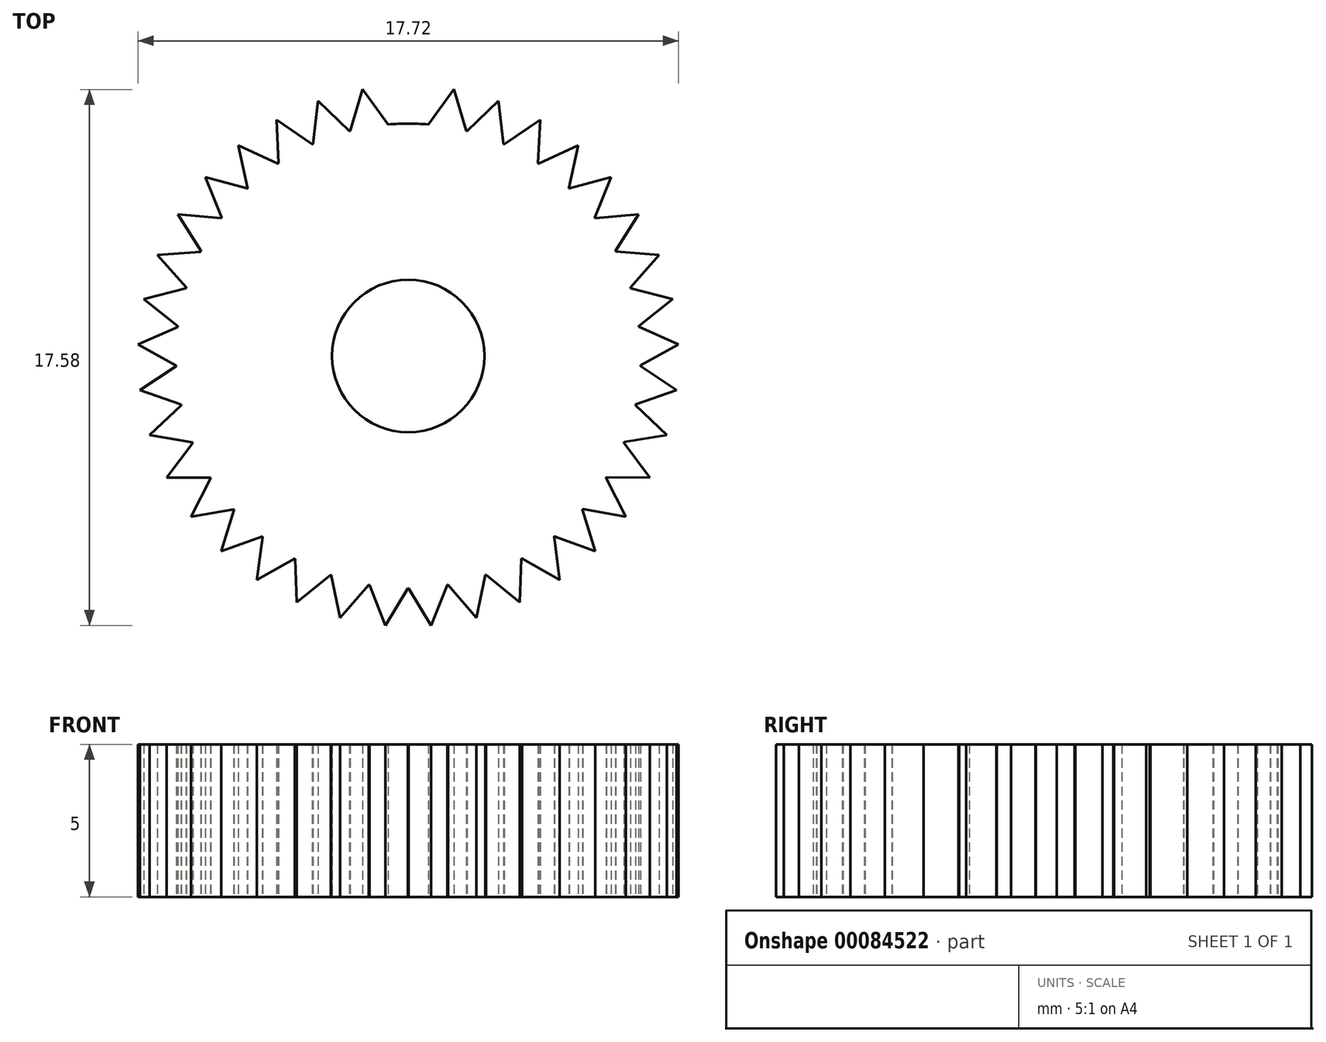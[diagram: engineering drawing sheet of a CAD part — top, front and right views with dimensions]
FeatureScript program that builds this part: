
annotation { "Feature Type Name" : "Feature", "Feature Type Description" : "" }
export const myFeature = defineFeature(function(context is Context, id is Id, definition is map)
    precondition{}
    {
        {
            var Q0;
            Q0=qCreatedBy(makeId("Top.planeOp"),FACE);
            var sketch = newSketch(context, id + "F0", { "sketchPlane" : qUnion([Q0])});
            skCircle(sketch, "E0", {"center": v(0, 0) * mm, "radius": 2.5 * mm});
            skPoint(sketch, "E1", {"position": v(0, 7.62) * mm});
            skLineSegment(sketch, "E2", {"start": v(0, 8.87) * mm, "end": v(-0.64, 7.6) * mm});
            skLineSegment(sketch, "E3", {"start": v(0, 8.87) * mm, "end": v(0.63, 7.6) * mm});
            skLineSegment(sketch, "E4.1.0", {"start": v(1.5, 8.74) * mm, "end": v(1.9, 7.38) * mm});
            skLineSegment(sketch, "E4.1.1", {"start": v(1.5, 8.74) * mm, "end": v(0.66, 7.6) * mm});
            skLineSegment(sketch, "E4.2.0", {"start": v(2.95, 8.36) * mm, "end": v(3.13, 6.95) * mm});
            skLineSegment(sketch, "E4.2.1", {"start": v(2.95, 8.36) * mm, "end": v(1.93, 7.37) * mm});
            skLineSegment(sketch, "E4.3.0", {"start": v(4.33, 7.74) * mm, "end": v(4.26, 6.32) * mm});
            skLineSegment(sketch, "E4.3.1", {"start": v(4.33, 7.74) * mm, "end": v(3.15, 6.94) * mm});
            skLineSegment(sketch, "E4.4.0", {"start": v(5.57, 6.9) * mm, "end": v(5.26, 5.51) * mm});
            skLineSegment(sketch, "E4.4.1", {"start": v(5.57, 6.9) * mm, "end": v(4.27, 6.3) * mm});
            skLineSegment(sketch, "E4.5.0", {"start": v(6.66, 5.86) * mm, "end": v(6.12, 4.54) * mm});
            skLineSegment(sketch, "E4.5.1", {"start": v(6.66, 5.86) * mm, "end": v(5.28, 5.5) * mm});
            skLineSegment(sketch, "E4.6.0", {"start": v(7.55, 4.65) * mm, "end": v(6.8, 3.44) * mm});
            skLineSegment(sketch, "E4.6.1", {"start": v(7.55, 4.65) * mm, "end": v(6.13, 4.52) * mm});
            skLineSegment(sketch, "E4.7.0", {"start": v(8.23, 3.3) * mm, "end": v(7.28, 2.24) * mm});
            skLineSegment(sketch, "E4.7.1", {"start": v(8.23, 3.3) * mm, "end": v(6.8, 3.42) * mm});
            skLineSegment(sketch, "E4.8.0", {"start": v(8.67, 1.87) * mm, "end": v(7.56, 0.98) * mm});
            skLineSegment(sketch, "E4.8.1", {"start": v(8.67, 1.87) * mm, "end": v(7.29, 2.22) * mm});
            skLineSegment(sketch, "E4.9.0", {"start": v(8.86, 0.38) * mm, "end": v(7.61, -0.3) * mm});
            skLineSegment(sketch, "E4.9.1", {"start": v(8.86, 0.38) * mm, "end": v(7.56, 0.96) * mm});
            skLineSegment(sketch, "E4.10.0", {"start": v(8.8, -1.13) * mm, "end": v(7.45, -1.6) * mm});
            skLineSegment(sketch, "E4.10.1", {"start": v(8.8, -1.13) * mm, "end": v(7.61, -0.33) * mm});
            skLineSegment(sketch, "E4.11.0", {"start": v(8.48, -2.6) * mm, "end": v(7.08, -2.83) * mm});
            skLineSegment(sketch, "E4.11.1", {"start": v(8.48, -2.6) * mm, "end": v(7.45, -1.61) * mm});
            skLineSegment(sketch, "E4.12.0", {"start": v(7.92, -4) * mm, "end": v(6.5, -3.98) * mm});
            skLineSegment(sketch, "E4.12.1", {"start": v(7.92, -4) * mm, "end": v(7.07, -2.85) * mm});
            skLineSegment(sketch, "E4.13.0", {"start": v(7.13, -5.27) * mm, "end": v(5.73, -5.02) * mm});
            skLineSegment(sketch, "E4.13.1", {"start": v(7.13, -5.27) * mm, "end": v(6.48, -4) * mm});
            skLineSegment(sketch, "E4.14.0", {"start": v(6.14, -6.4) * mm, "end": v(4.8, -5.92) * mm});
            skLineSegment(sketch, "E4.14.1", {"start": v(6.14, -6.4) * mm, "end": v(5.71, -5.04) * mm});
            skLineSegment(sketch, "E4.15.0", {"start": v(4.97, -7.35) * mm, "end": v(3.73, -6.65) * mm});
            skLineSegment(sketch, "E4.15.1", {"start": v(4.97, -7.35) * mm, "end": v(4.78, -5.93) * mm});
            skLineSegment(sketch, "E4.16.0", {"start": v(3.65, -8.08) * mm, "end": v(2.55, -7.18) * mm});
            skLineSegment(sketch, "E4.16.1", {"start": v(3.65, -8.08) * mm, "end": v(3.7, -6.66) * mm});
            skLineSegment(sketch, "E4.17.0", {"start": v(2.24, -8.58) * mm, "end": v(1.3, -7.5) * mm});
            skLineSegment(sketch, "E4.17.1", {"start": v(2.24, -8.58) * mm, "end": v(2.53, -7.19) * mm});
            skLineSegment(sketch, "E4.18.0", {"start": v(0.75, -8.84) * mm, "end": v(0.01, -7.62) * mm});
            skLineSegment(sketch, "E4.18.1", {"start": v(0.75, -8.84) * mm, "end": v(1.28, -7.51) * mm});
            skLineSegment(sketch, "E4.19.0", {"start": v(-0.75, -8.84) * mm, "end": v(-1.27, -7.51) * mm});
            skLineSegment(sketch, "E4.19.1", {"start": v(-0.75, -8.84) * mm, "end": v(0, -7.62) * mm});
            skLineSegment(sketch, "E4.20.0", {"start": v(-2.24, -8.58) * mm, "end": v(-2.53, -7.19) * mm});
            skLineSegment(sketch, "E4.20.1", {"start": v(-2.24, -8.58) * mm, "end": v(-1.3, -7.5) * mm});
            skLineSegment(sketch, "E4.21.0", {"start": v(-3.65, -8.08) * mm, "end": v(-3.7, -6.66) * mm});
            skLineSegment(sketch, "E4.21.1", {"start": v(-3.65, -8.08) * mm, "end": v(-2.55, -7.18) * mm});
            skLineSegment(sketch, "E4.22.0", {"start": v(-4.97, -7.35) * mm, "end": v(-4.78, -5.94) * mm});
            skLineSegment(sketch, "E4.22.1", {"start": v(-4.97, -7.35) * mm, "end": v(-3.72, -6.65) * mm});
            skLineSegment(sketch, "E4.23.0", {"start": v(-6.14, -6.4) * mm, "end": v(-5.71, -5.04) * mm});
            skLineSegment(sketch, "E4.23.1", {"start": v(-6.14, -6.4) * mm, "end": v(-4.8, -5.92) * mm});
            skLineSegment(sketch, "E4.24.0", {"start": v(-7.13, -5.27) * mm, "end": v(-6.48, -4) * mm});
            skLineSegment(sketch, "E4.24.1", {"start": v(-7.13, -5.27) * mm, "end": v(-5.73, -5.03) * mm});
            skLineSegment(sketch, "E4.25.0", {"start": v(-7.92, -4) * mm, "end": v(-7.07, -2.85) * mm});
            skLineSegment(sketch, "E4.25.1", {"start": v(-7.92, -4) * mm, "end": v(-6.5, -3.99) * mm});
            skLineSegment(sketch, "E4.26.0", {"start": v(-8.48, -2.6) * mm, "end": v(-7.45, -1.62) * mm});
            skLineSegment(sketch, "E4.26.1", {"start": v(-8.48, -2.6) * mm, "end": v(-7.07, -2.83) * mm});
            skLineSegment(sketch, "E4.27.0", {"start": v(-8.8, -1.13) * mm, "end": v(-7.61, -0.34) * mm});
            skLineSegment(sketch, "E4.27.1", {"start": v(-8.8, -1.13) * mm, "end": v(-7.45, -1.6) * mm});
            skLineSegment(sketch, "E4.28.0", {"start": v(-8.86, 0.38) * mm, "end": v(-7.56, 0.95) * mm});
            skLineSegment(sketch, "E4.28.1", {"start": v(-8.86, 0.38) * mm, "end": v(-7.61, -0.31) * mm});
            skLineSegment(sketch, "E4.29.0", {"start": v(-8.67, 1.87) * mm, "end": v(-7.29, 2.22) * mm});
            skLineSegment(sketch, "E4.29.1", {"start": v(-8.67, 1.87) * mm, "end": v(-7.56, 0.98) * mm});
            skLineSegment(sketch, "E4.30.0", {"start": v(-8.23, 3.3) * mm, "end": v(-6.81, 3.42) * mm});
            skLineSegment(sketch, "E4.30.1", {"start": v(-8.23, 3.3) * mm, "end": v(-7.28, 2.24) * mm});
            skLineSegment(sketch, "E4.31.0", {"start": v(-7.55, 4.65) * mm, "end": v(-6.13, 4.52) * mm});
            skLineSegment(sketch, "E4.31.1", {"start": v(-7.55, 4.65) * mm, "end": v(-6.8, 3.44) * mm});
            skLineSegment(sketch, "E4.32.0", {"start": v(-6.66, 5.86) * mm, "end": v(-5.28, 5.5) * mm});
            skLineSegment(sketch, "E4.32.1", {"start": v(-6.66, 5.86) * mm, "end": v(-6.12, 4.54) * mm});
            skLineSegment(sketch, "E4.33.0", {"start": v(-5.57, 6.9) * mm, "end": v(-4.28, 6.3) * mm});
            skLineSegment(sketch, "E4.33.1", {"start": v(-5.57, 6.9) * mm, "end": v(-5.27, 5.5) * mm});
            skLineSegment(sketch, "E4.34.0", {"start": v(-4.33, 7.74) * mm, "end": v(-3.15, 6.94) * mm});
            skLineSegment(sketch, "E4.34.1", {"start": v(-4.33, 7.74) * mm, "end": v(-4.26, 6.32) * mm});
            skLineSegment(sketch, "E4.35.0", {"start": v(-2.95, 8.36) * mm, "end": v(-1.93, 7.37) * mm});
            skLineSegment(sketch, "E4.35.1", {"start": v(-2.95, 8.36) * mm, "end": v(-3.13, 6.95) * mm});
            skLineSegment(sketch, "E4.36.0", {"start": v(-1.5, 8.74) * mm, "end": v(-0.66, 7.6) * mm});
            skLineSegment(sketch, "E4.36.1", {"start": v(-1.5, 8.74) * mm, "end": v(-1.91, 7.38) * mm});
            skCircle(sketch, "E5", {"center": v(0, 0) * mm, "radius": 7.62 * mm});
            skLineSegment(sketch, "E6", {"start": v(-0.64, 7.6) * mm, "end": v(0, 8.87) * mm});
            skSolve(sketch);
        }
        {
            var Q0;
            Q0=makeQuery(id+"F0.imprint","IMPRINT",FACE,{"disambiguationData":[TD([[makeQuery(id+"F0.imprint","IMPRINT",EDGE,{"derivedFrom":sQuery(id+"F0.wireOp",EDGE,"E0")}),-1.0]])]});
            var Q1;
            {var subQ0=sQuery(id+"F0.wireOp",EDGE,"E4.32.0");Q1=makeQuery(id+"F0.imprint","IMPRINT",FACE,{"disambiguationData":[TD([[makeQuery(id+"F0.imprint","IMPRINT",EDGE,{"derivedFrom":subQ0}),-1.0]])]});}
            var Q2;
            {var subQ0=sQuery(id+"F0.wireOp",EDGE,"E4.33.0");Q2=makeQuery(id+"F0.imprint","IMPRINT",FACE,{"disambiguationData":[TD([[makeQuery(id+"F0.imprint","IMPRINT",EDGE,{"derivedFrom":subQ0}),-1.0]])]});}
            var Q3;
            {var subQ0=sQuery(id+"F0.wireOp",EDGE,"E4.34.0");Q3=makeQuery(id+"F0.imprint","IMPRINT",FACE,{"disambiguationData":[TD([[makeQuery(id+"F0.imprint","IMPRINT",EDGE,{"derivedFrom":subQ0}),-1.0]])]});}
            var Q4;
            {var subQ0=sQuery(id+"F0.wireOp",EDGE,"E4.35.0");Q4=makeQuery(id+"F0.imprint","IMPRINT",FACE,{"disambiguationData":[TD([[makeQuery(id+"F0.imprint","IMPRINT",EDGE,{"derivedFrom":subQ0}),-1.0]])]});}
            var Q5;
            {var subQ0=sQuery(id+"F0.wireOp",EDGE,"E4.36.0");Q5=makeQuery(id+"F0.imprint","IMPRINT",FACE,{"disambiguationData":[TD([[makeQuery(id+"F0.imprint","IMPRINT",EDGE,{"derivedFrom":subQ0}),-1.0]])]});}
            var Q6;
            {var subQ0=sQuery(id+"F0.wireOp",EDGE,"E4.1.0");Q6=makeQuery(id+"F0.imprint","IMPRINT",FACE,{"disambiguationData":[TD([[makeQuery(id+"F0.imprint","IMPRINT",EDGE,{"derivedFrom":subQ0}),-1.0]])]});}
            var Q7;
            {var subQ0=sQuery(id+"F0.wireOp",EDGE,"E4.2.0");Q7=makeQuery(id+"F0.imprint","IMPRINT",FACE,{"disambiguationData":[TD([[makeQuery(id+"F0.imprint","IMPRINT",EDGE,{"derivedFrom":subQ0}),-1.0]])]});}
            var Q8;
            {var subQ0=sQuery(id+"F0.wireOp",EDGE,"pScTJWKr-x1fD-1paM-wDNM-PNdl5gfp4UO0");Q8=makeQuery(id+"F0.imprint","IMPRINT",FACE,{"disambiguationData":[TD([[makeQuery(id+"F0.imprint","IMPRINT",EDGE,{"derivedFrom":subQ0}),-1.0]])]});}
            var Q9;
            {var subQ0=sQuery(id+"F0.wireOp",EDGE,"pScTJWKr-x1fD-1paM-wDNM-PNdl5gfp4UO0");Q9=makeQuery(id+"F0.imprint","IMPRINT",FACE,{"disambiguationData":[TD([[makeQuery(id+"F0.imprint","IMPRINT",EDGE,{"derivedFrom":subQ0}),1.0]])]});}
            var Q10;
            {var subQ0=sQuery(id+"F0.wireOp",EDGE,"E4.3.0");Q10=makeQuery(id+"F0.imprint","IMPRINT",FACE,{"disambiguationData":[TD([[makeQuery(id+"F0.imprint","IMPRINT",EDGE,{"derivedFrom":subQ0}),-1.0]])]});}
            var Q11;
            {var subQ0=sQuery(id+"F0.wireOp",EDGE,"E4.4.0");Q11=makeQuery(id+"F0.imprint","IMPRINT",FACE,{"disambiguationData":[TD([[makeQuery(id+"F0.imprint","IMPRINT",EDGE,{"derivedFrom":subQ0}),-1.0]])]});}
            var Q12;
            {var subQ0=sQuery(id+"F0.wireOp",EDGE,"E4.5.0");Q12=makeQuery(id+"F0.imprint","IMPRINT",FACE,{"disambiguationData":[TD([[makeQuery(id+"F0.imprint","IMPRINT",EDGE,{"derivedFrom":subQ0}),-1.0]])]});}
            var Q13;
            {var subQ0=sQuery(id+"F0.wireOp",EDGE,"E4.6.0");Q13=makeQuery(id+"F0.imprint","IMPRINT",FACE,{"disambiguationData":[TD([[makeQuery(id+"F0.imprint","IMPRINT",EDGE,{"derivedFrom":subQ0}),-1.0]])]});}
            var Q14;
            {var subQ1=sQuery(id+"F0.wireOp",EDGE,"E4.7.0");Q14=makeQuery(id+"F0.imprint","IMPRINT",FACE,{"disambiguationData":[TD([[makeQuery(id+"F0.imprint","IMPRINT",EDGE,{"derivedFrom":subQ1}),-1.0]])]});}
            var Q15;
            {var subQ0=sQuery(id+"F0.wireOp",EDGE,"E4.8.0");Q15=makeQuery(id+"F0.imprint","IMPRINT",FACE,{"disambiguationData":[TD([[makeQuery(id+"F0.imprint","IMPRINT",EDGE,{"derivedFrom":subQ0}),-1.0]])]});}
            var Q16;
            {var subQ1=sQuery(id+"F0.wireOp",EDGE,"E4.9.0");Q16=makeQuery(id+"F0.imprint","IMPRINT",FACE,{"disambiguationData":[TD([[makeQuery(id+"F0.imprint","IMPRINT",EDGE,{"derivedFrom":subQ1}),-1.0]])]});}
            var Q17;
            {var subQ1=sQuery(id+"F0.wireOp",EDGE,"E4.10.0");Q17=makeQuery(id+"F0.imprint","IMPRINT",FACE,{"disambiguationData":[TD([[makeQuery(id+"F0.imprint","IMPRINT",EDGE,{"derivedFrom":subQ1}),-1.0]])]});}
            var Q18;
            {var subQ0=sQuery(id+"F0.wireOp",EDGE,"E4.11.0");Q18=makeQuery(id+"F0.imprint","IMPRINT",FACE,{"disambiguationData":[TD([[makeQuery(id+"F0.imprint","IMPRINT",EDGE,{"derivedFrom":subQ0}),-1.0]])]});}
            var Q19;
            {var subQ1=sQuery(id+"F0.wireOp",EDGE,"E4.12.0");Q19=makeQuery(id+"F0.imprint","IMPRINT",FACE,{"disambiguationData":[TD([[makeQuery(id+"F0.imprint","IMPRINT",EDGE,{"derivedFrom":subQ1}),-1.0]])]});}
            var Q20;
            {var subQ0=sQuery(id+"F0.wireOp",EDGE,"E4.13.0");Q20=makeQuery(id+"F0.imprint","IMPRINT",FACE,{"disambiguationData":[TD([[makeQuery(id+"F0.imprint","IMPRINT",EDGE,{"derivedFrom":subQ0}),-1.0]])]});}
            var Q21;
            {var subQ0=sQuery(id+"F0.wireOp",EDGE,"E4.14.0");Q21=makeQuery(id+"F0.imprint","IMPRINT",FACE,{"disambiguationData":[TD([[makeQuery(id+"F0.imprint","IMPRINT",EDGE,{"derivedFrom":subQ0}),-1.0]])]});}
            var Q22;
            {var subQ0=sQuery(id+"F0.wireOp",EDGE,"E4.15.0");Q22=makeQuery(id+"F0.imprint","IMPRINT",FACE,{"disambiguationData":[TD([[makeQuery(id+"F0.imprint","IMPRINT",EDGE,{"derivedFrom":subQ0}),-1.0]])]});}
            var Q23;
            {var subQ0=sQuery(id+"F0.wireOp",EDGE,"E4.16.0");Q23=makeQuery(id+"F0.imprint","IMPRINT",FACE,{"disambiguationData":[TD([[makeQuery(id+"F0.imprint","IMPRINT",EDGE,{"derivedFrom":subQ0}),-1.0]])]});}
            var Q24;
            {var subQ0=sQuery(id+"F0.wireOp",EDGE,"E4.17.0");Q24=makeQuery(id+"F0.imprint","IMPRINT",FACE,{"disambiguationData":[TD([[makeQuery(id+"F0.imprint","IMPRINT",EDGE,{"derivedFrom":subQ0}),-1.0]])]});}
            var Q25;
            {var subQ0=sQuery(id+"F0.wireOp",EDGE,"E4.18.0");Q25=makeQuery(id+"F0.imprint","IMPRINT",FACE,{"disambiguationData":[TD([[makeQuery(id+"F0.imprint","IMPRINT",EDGE,{"derivedFrom":subQ0}),-1.0]])]});}
            var Q26;
            {var subQ0=sQuery(id+"F0.wireOp",EDGE,"E4.19.0");Q26=makeQuery(id+"F0.imprint","IMPRINT",FACE,{"disambiguationData":[TD([[makeQuery(id+"F0.imprint","IMPRINT",EDGE,{"derivedFrom":subQ0}),-1.0]])]});}
            var Q27;
            {var subQ1=sQuery(id+"F0.wireOp",EDGE,"E4.20.0");Q27=makeQuery(id+"F0.imprint","IMPRINT",FACE,{"disambiguationData":[TD([[makeQuery(id+"F0.imprint","IMPRINT",EDGE,{"derivedFrom":subQ1}),-1.0]])]});}
            var Q28;
            {var subQ0=sQuery(id+"F0.wireOp",EDGE,"E4.21.0");Q28=makeQuery(id+"F0.imprint","IMPRINT",FACE,{"disambiguationData":[TD([[makeQuery(id+"F0.imprint","IMPRINT",EDGE,{"derivedFrom":subQ0}),-1.0]])]});}
            var Q29;
            {var subQ0=sQuery(id+"F0.wireOp",EDGE,"E4.22.0");Q29=makeQuery(id+"F0.imprint","IMPRINT",FACE,{"disambiguationData":[TD([[makeQuery(id+"F0.imprint","IMPRINT",EDGE,{"derivedFrom":subQ0}),-1.0]])]});}
            var Q30;
            {var subQ0=sQuery(id+"F0.wireOp",EDGE,"E4.23.0");Q30=makeQuery(id+"F0.imprint","IMPRINT",FACE,{"disambiguationData":[TD([[makeQuery(id+"F0.imprint","IMPRINT",EDGE,{"derivedFrom":subQ0}),-1.0]])]});}
            var Q31;
            {var subQ0=sQuery(id+"F0.wireOp",EDGE,"E4.24.0");Q31=makeQuery(id+"F0.imprint","IMPRINT",FACE,{"disambiguationData":[TD([[makeQuery(id+"F0.imprint","IMPRINT",EDGE,{"derivedFrom":subQ0}),-1.0]])]});}
            var Q32;
            {var subQ0=sQuery(id+"F0.wireOp",EDGE,"E4.25.0");Q32=makeQuery(id+"F0.imprint","IMPRINT",FACE,{"disambiguationData":[TD([[makeQuery(id+"F0.imprint","IMPRINT",EDGE,{"derivedFrom":subQ0}),-1.0]])]});}
            var Q33;
            {var subQ1=sQuery(id+"F0.wireOp",EDGE,"E4.26.0");Q33=makeQuery(id+"F0.imprint","IMPRINT",FACE,{"disambiguationData":[TD([[makeQuery(id+"F0.imprint","IMPRINT",EDGE,{"derivedFrom":subQ1}),-1.0]])]});}
            var Q34;
            {var subQ0=sQuery(id+"F0.wireOp",EDGE,"E4.27.0");Q34=makeQuery(id+"F0.imprint","IMPRINT",FACE,{"disambiguationData":[TD([[makeQuery(id+"F0.imprint","IMPRINT",EDGE,{"derivedFrom":subQ0}),-1.0]])]});}
            var Q35;
            {var subQ0=sQuery(id+"F0.wireOp",EDGE,"E4.28.0");Q35=makeQuery(id+"F0.imprint","IMPRINT",FACE,{"disambiguationData":[TD([[makeQuery(id+"F0.imprint","IMPRINT",EDGE,{"derivedFrom":subQ0}),-1.0]])]});}
            var Q36;
            {var subQ0=sQuery(id+"F0.wireOp",EDGE,"E4.29.0");Q36=makeQuery(id+"F0.imprint","IMPRINT",FACE,{"disambiguationData":[TD([[makeQuery(id+"F0.imprint","IMPRINT",EDGE,{"derivedFrom":subQ0}),-1.0]])]});}
            var Q37;
            {var subQ0=sQuery(id+"F0.wireOp",EDGE,"E4.30.0");Q37=makeQuery(id+"F0.imprint","IMPRINT",FACE,{"disambiguationData":[TD([[makeQuery(id+"F0.imprint","IMPRINT",EDGE,{"derivedFrom":subQ0}),-1.0]])]});}
            var Q38;
            {var subQ0=sQuery(id+"F0.wireOp",EDGE,"E4.31.0");Q38=makeQuery(id+"F0.imprint","IMPRINT",FACE,{"disambiguationData":[TD([[makeQuery(id+"F0.imprint","IMPRINT",EDGE,{"derivedFrom":subQ0}),-1.0]])]});}
            var Q39;
            {var subQ0=sQuery(id+"F0.wireOp",EDGE,"E6");Q39=makeQuery(id+"F0.imprint","IMPRINT",FACE,{"disambiguationData":[TD([[makeQuery(id+"F0.imprint","IMPRINT",EDGE,{"derivedFrom":subQ0}),-1.0]])]});}
            extrude(context, id + "F1", {"entities" : qUnion([Q0, Q1, Q2, Q3, Q4, Q5, Q6, Q7, Q8, Q9, Q10, Q11, Q12, Q13, Q14, Q15, Q16, Q17, Q18, Q19, Q20, Q21, Q22, Q23, Q24, Q25, Q26, Q27, Q28, Q29, Q30, Q31, Q32, Q33, Q34, Q35, Q36, Q37, Q38, Q39]), "depth" : 5 * mm});
        }
    });
